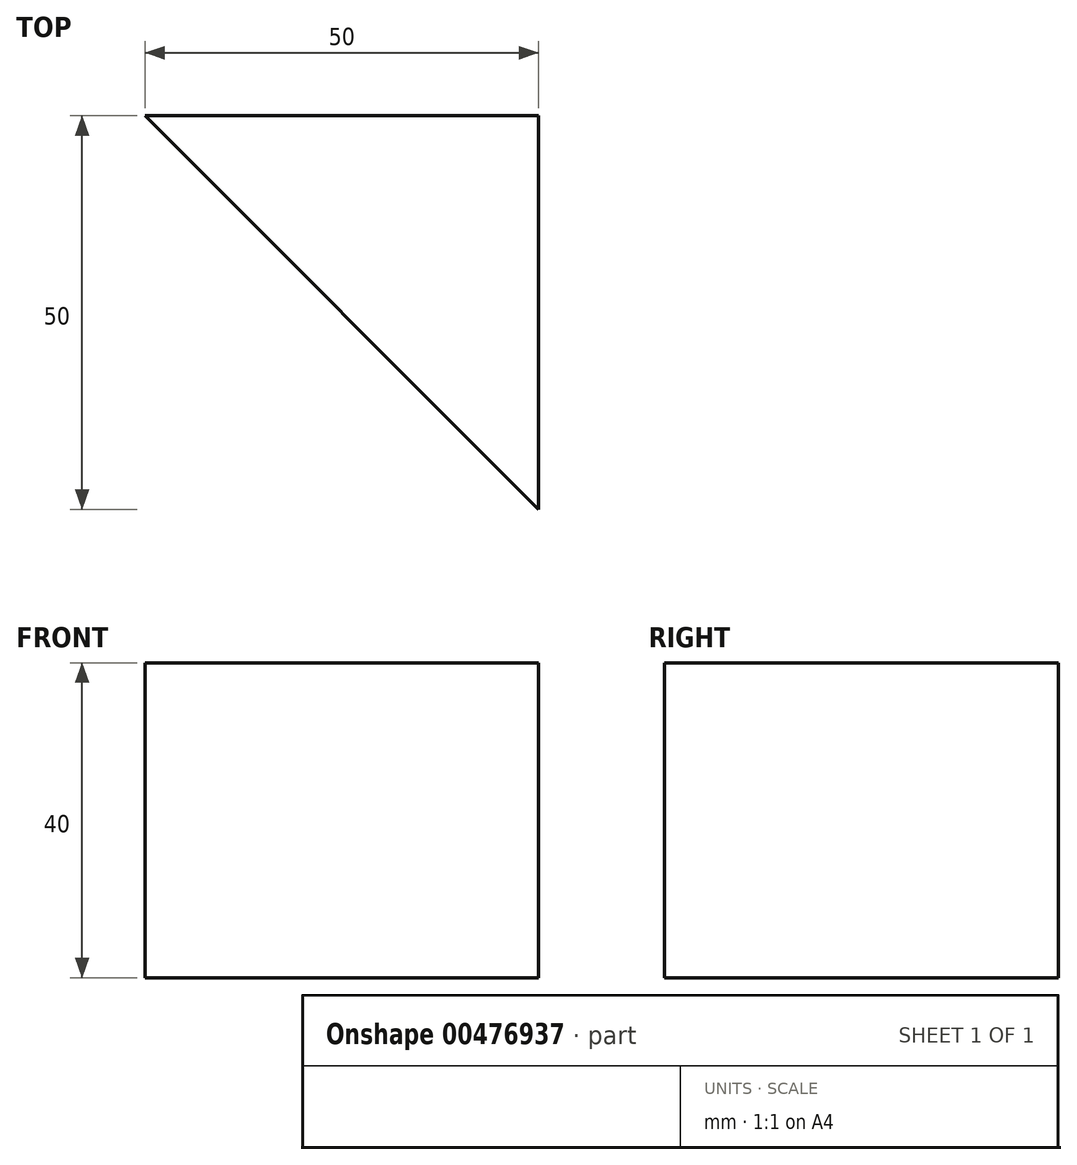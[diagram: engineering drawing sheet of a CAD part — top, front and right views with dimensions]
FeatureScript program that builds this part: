
annotation { "Feature Type Name" : "Feature", "Feature Type Description" : "" }
export const myFeature = defineFeature(function(context is Context, id is Id, definition is map)
    precondition{}
    {
        {
            var Q0;
            Q0=qCreatedBy(makeId("Top.planeOp"),FACE);
            var sketch = newSketch(context, id + "F0", { "sketchPlane" : qUnion([Q0])});
            skLineSegment(sketch, "E0", {"start": v(0, 0) * mm, "end": v(50, 0) * mm});
            skLineSegment(sketch, "E1", {"start": v(50, 0) * mm, "end": v(50, -50) * mm});
            skLineSegment(sketch, "E2", {"start": v(50, -50) * mm, "end": v(0, 0) * mm});
            skSolve(sketch);
        }
        {
            var Q0;
            Q0=makeQuery(id+"F0.imprint","IMPRINT",FACE,{"disambiguationData":[TD([[makeQuery(id+"F0.imprint","IMPRINT",EDGE,{"derivedFrom":sQuery(id+"F0.wireOp",EDGE,"E0")}),-1.0]])]});
            extrude(context, id + "F1", {"entities" : qUnion([Q0]), "depth" : 40 * mm});
        }
    });
